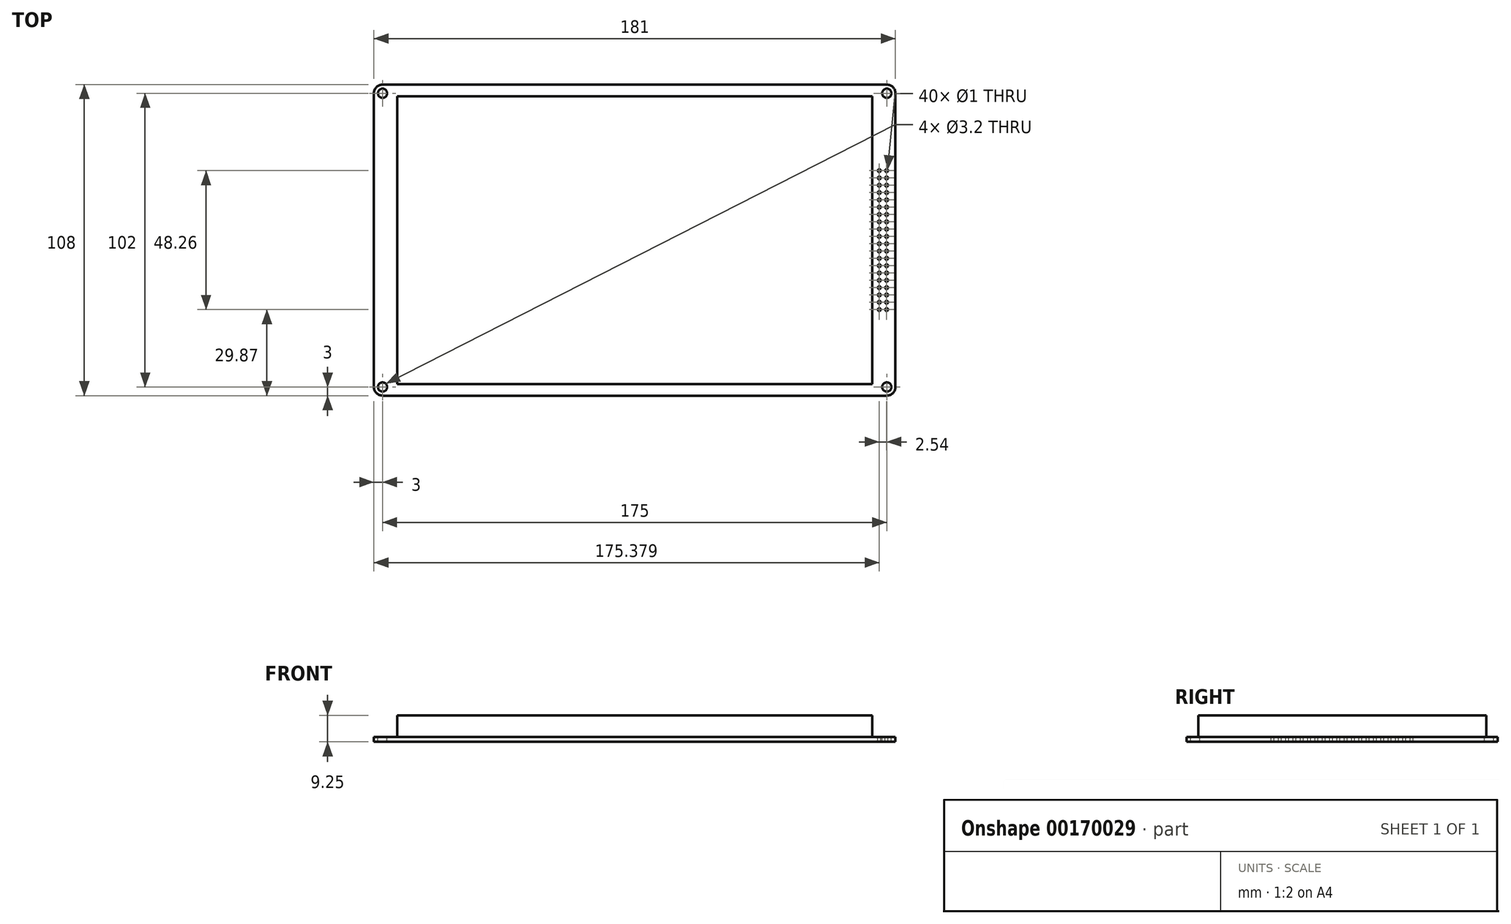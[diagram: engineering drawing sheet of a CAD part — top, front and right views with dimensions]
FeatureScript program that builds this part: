
annotation { "Feature Type Name" : "Feature", "Feature Type Description" : "" }
export const myFeature = defineFeature(function(context is Context, id is Id, definition is map)
    precondition{}
    {
        {
            var Q0;
            Q0=qCreatedBy(makeId("Top.planeOp"),FACE);
            var sketch = newSketch(context, id + "F0", { "sketchPlane" : qUnion([Q0])});
            skLineSegment(sketch, "E0.bottom", {"start": v(3, 0) * mm, "end": v(178, 0) * mm});
            skLineSegment(sketch, "E0.top", {"start": v(3, 108) * mm, "end": v(178, 108) * mm});
            skLineSegment(sketch, "E0.left", {"start": v(0, 3) * mm, "end": v(0, 105) * mm});
            skLineSegment(sketch, "E0.right", {"start": v(181, 3) * mm, "end": v(181, 105) * mm});
            skLineSegment(sketch, "E1.bottom", {"start": v(8.05, 4) * mm, "end": v(172.95, 4) * mm});
            skLineSegment(sketch, "E1.top", {"start": v(8.05, 104) * mm, "end": v(172.95, 104) * mm});
            skLineSegment(sketch, "E1.left", {"start": v(8.05, 4) * mm, "end": v(8.05, 104) * mm});
            skLineSegment(sketch, "E1.right", {"start": v(172.95, 4) * mm, "end": v(172.95, 104) * mm});
            skCircle(sketch, "E2", {"center": v(3, 105) * mm, "radius": 1.6 * mm});
            skCircle(sketch, "E3", {"center": v(3, 3) * mm, "radius": 1.6 * mm});
            skCircle(sketch, "E4", {"center": v(178, 3) * mm, "radius": 1.6 * mm});
            skCircle(sketch, "E5", {"center": v(178, 105) * mm, "radius": 1.6 * mm});
            skPoint(sketch, "E6.visualSharp", {"position": v(0, 108) * mm});
            skArc(sketch, "E6.filletArc", {"start": v(3, 108) * mm, "mid": v(0.88, 107.12) * mm, "end": v(0, 105) * mm});
            skPoint(sketch, "E7.visualSharp", {"position": v(181, 108) * mm});
            skArc(sketch, "E7.filletArc", {"start": v(181, 105) * mm, "mid": v(180.12, 107.12) * mm, "end": v(178, 108) * mm});
            skPoint(sketch, "E8.visualSharp", {"position": v(181, 0) * mm});
            skArc(sketch, "E8.filletArc", {"start": v(178, 0) * mm, "mid": v(180.12, 0.88) * mm, "end": v(181, 3) * mm});
            skPoint(sketch, "E9.visualSharp", {"position": v(0, 0) * mm});
            skArc(sketch, "E9.filletArc", {"start": v(0, 3) * mm, "mid": v(0.88, 0.88) * mm, "end": v(3, 0) * mm});
            skCircle(sketch, "E10", {"center": v(177.92, 78.13) * mm, "radius": 0.5 * mm});
            skCircle(sketch, "E11", {"center": v(175.38, 78.13) * mm, "radius": 0.5 * mm});
            skCircle(sketch, "E12.1.0.0", {"center": v(175.38, 75.59) * mm, "radius": 0.5 * mm});
            skCircle(sketch, "E12.1.0.1", {"center": v(177.92, 75.59) * mm, "radius": 0.5 * mm});
            skCircle(sketch, "E12.2.0.0", {"center": v(175.38, 73.05) * mm, "radius": 0.5 * mm});
            skCircle(sketch, "E12.2.0.1", {"center": v(177.92, 73.05) * mm, "radius": 0.5 * mm});
            skCircle(sketch, "E12.3.0.0", {"center": v(175.38, 70.5) * mm, "radius": 0.5 * mm});
            skCircle(sketch, "E12.3.0.1", {"center": v(177.92, 70.5) * mm, "radius": 0.5 * mm});
            skCircle(sketch, "E12.4.0.0", {"center": v(175.38, 67.97) * mm, "radius": 0.5 * mm});
            skCircle(sketch, "E12.4.0.1", {"center": v(177.92, 67.97) * mm, "radius": 0.5 * mm});
            skCircle(sketch, "E12.5.0.0", {"center": v(175.38, 65.43) * mm, "radius": 0.5 * mm});
            skCircle(sketch, "E12.5.0.1", {"center": v(177.92, 65.43) * mm, "radius": 0.5 * mm});
            skCircle(sketch, "E12.6.0.0", {"center": v(175.38, 62.89) * mm, "radius": 0.5 * mm});
            skCircle(sketch, "E12.6.0.1", {"center": v(177.92, 62.89) * mm, "radius": 0.5 * mm});
            skCircle(sketch, "E12.7.0.0", {"center": v(175.38, 60.35) * mm, "radius": 0.5 * mm});
            skCircle(sketch, "E12.7.0.1", {"center": v(177.92, 60.35) * mm, "radius": 0.5 * mm});
            skCircle(sketch, "E12.8.0.0", {"center": v(175.38, 57.8) * mm, "radius": 0.5 * mm});
            skCircle(sketch, "E12.8.0.1", {"center": v(177.92, 57.8) * mm, "radius": 0.5 * mm});
            skCircle(sketch, "E12.9.0.0", {"center": v(175.38, 55.27) * mm, "radius": 0.5 * mm});
            skCircle(sketch, "E12.9.0.1", {"center": v(177.92, 55.27) * mm, "radius": 0.5 * mm});
            skCircle(sketch, "E12.10.0.0", {"center": v(175.38, 52.73) * mm, "radius": 0.5 * mm});
            skCircle(sketch, "E12.10.0.1", {"center": v(177.92, 52.73) * mm, "radius": 0.5 * mm});
            skCircle(sketch, "E12.11.0.0", {"center": v(175.38, 50.19) * mm, "radius": 0.5 * mm});
            skCircle(sketch, "E12.11.0.1", {"center": v(177.92, 50.19) * mm, "radius": 0.5 * mm});
            skCircle(sketch, "E12.12.0.0", {"center": v(175.38, 47.65) * mm, "radius": 0.5 * mm});
            skCircle(sketch, "E12.12.0.1", {"center": v(177.92, 47.65) * mm, "radius": 0.5 * mm});
            skCircle(sketch, "E12.13.0.0", {"center": v(175.38, 45.1) * mm, "radius": 0.5 * mm});
            skCircle(sketch, "E12.13.0.1", {"center": v(177.92, 45.1) * mm, "radius": 0.5 * mm});
            skCircle(sketch, "E12.14.0.0", {"center": v(175.38, 42.57) * mm, "radius": 0.5 * mm});
            skCircle(sketch, "E12.14.0.1", {"center": v(177.92, 42.57) * mm, "radius": 0.5 * mm});
            skCircle(sketch, "E12.15.0.0", {"center": v(175.38, 40.03) * mm, "radius": 0.5 * mm});
            skCircle(sketch, "E12.15.0.1", {"center": v(177.92, 40.03) * mm, "radius": 0.5 * mm});
            skCircle(sketch, "E12.16.0.0", {"center": v(175.38, 37.49) * mm, "radius": 0.5 * mm});
            skCircle(sketch, "E12.16.0.1", {"center": v(177.92, 37.49) * mm, "radius": 0.5 * mm});
            skCircle(sketch, "E12.17.0.0", {"center": v(175.38, 34.95) * mm, "radius": 0.5 * mm});
            skCircle(sketch, "E12.17.0.1", {"center": v(177.92, 34.95) * mm, "radius": 0.5 * mm});
            skCircle(sketch, "E12.18.0.0", {"center": v(175.38, 32.4) * mm, "radius": 0.5 * mm});
            skCircle(sketch, "E12.18.0.1", {"center": v(177.92, 32.4) * mm, "radius": 0.5 * mm});
            skCircle(sketch, "E12.19.0.0", {"center": v(175.38, 29.87) * mm, "radius": 0.5 * mm});
            skCircle(sketch, "E12.19.0.1", {"center": v(177.92, 29.87) * mm, "radius": 0.5 * mm});
            skLineSegment(sketch, "E12.direction1", {"start": v(175.38, 78.13) * mm, "end": v(175.38, 75.59) * mm, "construction": true});
            skSolve(sketch);
        }
        {
            var Q0;
            Q0=makeQuery(id+"F0.imprint","IMPRINT",FACE,{"disambiguationData":[TD([[makeQuery(id+"F0.imprint","IMPRINT",EDGE,{"derivedFrom":sQuery(id+"F0.wireOp",EDGE,"E0.bottom")}),1.0]])]});
            var Q1;
            Q1=makeQuery(id+"F0.imprint","IMPRINT",FACE,{"disambiguationData":[TD([[makeQuery(id+"F0.imprint","IMPRINT",EDGE,{"derivedFrom":sQuery(id+"F0.wireOp",EDGE,"E1.bottom")}),1.0]])]});
            extrude(context, id + "F1", {"entities" : qUnion([Q0, Q1]), "oppositeDirection" : true, "depth" : 1.75 * mm});
        }
        {
            var Q0;
            Q0=makeQuery(id+"F0.imprint","IMPRINT",FACE,{"disambiguationData":[TD([[makeQuery(id+"F0.imprint","IMPRINT",EDGE,{"derivedFrom":sQuery(id+"F0.wireOp",EDGE,"E1.bottom")}),1.0]])]});
            extrude(context, id + "F2", {"entities" : qUnion([Q0]), "operationType" : NewBodyOperationType.ADD, "depth" : 7.5 * mm});
        }
    });
